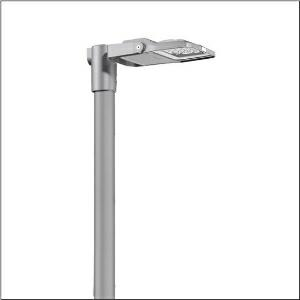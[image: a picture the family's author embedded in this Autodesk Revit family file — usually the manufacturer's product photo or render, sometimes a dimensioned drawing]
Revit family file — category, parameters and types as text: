
# Revit family: floodlight_fl_21_iq_micro___pl52_5xa7761a4d3a_5d98
name_source: partatom
category: Lighting Fixtures
units: mm (PartAtom-declared; Revit-internal decimal feet)

## family parameters
Cut with Voids When Loaded = No
Host = Face
Light Source = No
Part Type = Normal
Room Calculation Point = No
Round Connector Dimension = Use Diameter
Shared = No

## types (1)
- --- (1 x LED, 3010 lm, 23.1 W, 4000K)
    Apparent Load = 23 VA
    CIE Flux Codes = 26 60 98 100 100
    Color Rendering = 70
    Color Temperature = 4000K
    Default Elevation = 1800 mm
    Description = Floodlight FL 21 iQ micro, floodlight, primary light control with lens, of PMMA, primary optical cover: protective disc, of toughened safety glass, transparent, light distribution: PL52, light emission: direct distribution, installation type: surface-mounted, LED, High Power LED, rated luminous flux: 3.010lm, luminous efficacy: 130lm/W, light colour: 740, colour temperature: 4000K, control gear: iQ Comfort/DALI, control: optimised constant luminous flux control (CLO 2.0), Desk-Remote (wireless, voltage-free reading and setting of iQ features in the workshop via application-optimized NFC function/RFID function), Light-Fading, Smart-Wire, Night-Set, Lumen-Switch, Temp-Guard, Auto-Match, with terminal, 6-pole, mains connection: 220..240V, AC, 50/60Hz, start of lifetime: 23W, end of service life: 24W, reduction: 11W, luminaire housing, of diecast aluminium, powder-coated, Siteco® metallic grey (DB 702S), corrosivity category C5 mid according to DIN EN ISO 12944, suitable for swimming pools, chlorine-resistant, sealing non-destructively replaceable, please order mast flange separately, mast bracket, of steel, galvanised, powder-coated, Siteco® metallic grey (DB 702S), protection rating (complete): IP66, insulation class (complete): insulation class II (safety insulation), certification: CE, ENEC, VDE, protection symbol: D, impact resistance: IK07, permissible operating ambient temperature: -40..+40°C, permissible operating ambient temperature for outdoor applications: -40..+50°C, standard: DIN EN 12944, LABS conformity tested according to VDMA 24364:2018-05, packaging unit: 1 piece

Light Distribution: PL52
    Height = 65 mm
    Lamp = 1 x LED
    Lamp Light Flux = 3010 lm
    Lamp Power = 23.1 W
    Lamp count = 1
    Length = 312 mm
    Luminous efficacy = 130 lm/W
    Manufacturer = Siteco
    ModVariant = No
    Model = 5XA7761A4D3A
    Number of Poles = 1
    OnlyDefault = Yes
    Power Factor = 1
    Product Name = Floodlight FL 21 iQ micro | PL52
    Product group = floodlight | pylon annexe
    ProductGroupID = 6200
    Protection Class = Protection class II
    Protection Degree = IP 66
    RLX_Detail_Level = 1
    RLX_Emergency_Light_Flux = 0 lm
    RLX_Emergency_Type = 0
    RLX_Emergency_Type_DB = No
    RlxData = <blob elided: 102165 chars, md5=b584a59c>
    Socket = socket
    Standby Power = 0 W
    System Light Flux = 3010 lm
    System Power = 23 W
    Type Comments = factory setting: luminous flux: 100 % | dim-lin: 254 | 455 mA
    Type Image = l_1007121.jpg
    URL = http://relux.com
    VarID = @adj_177990
    Voltage = 0 V
    Weight = 0.00 kg
    Width = 230 mm

## geometry (parser evidence)
native form markers: Blend x4, Sweep x10
no freeform markers — native parametric forms only
